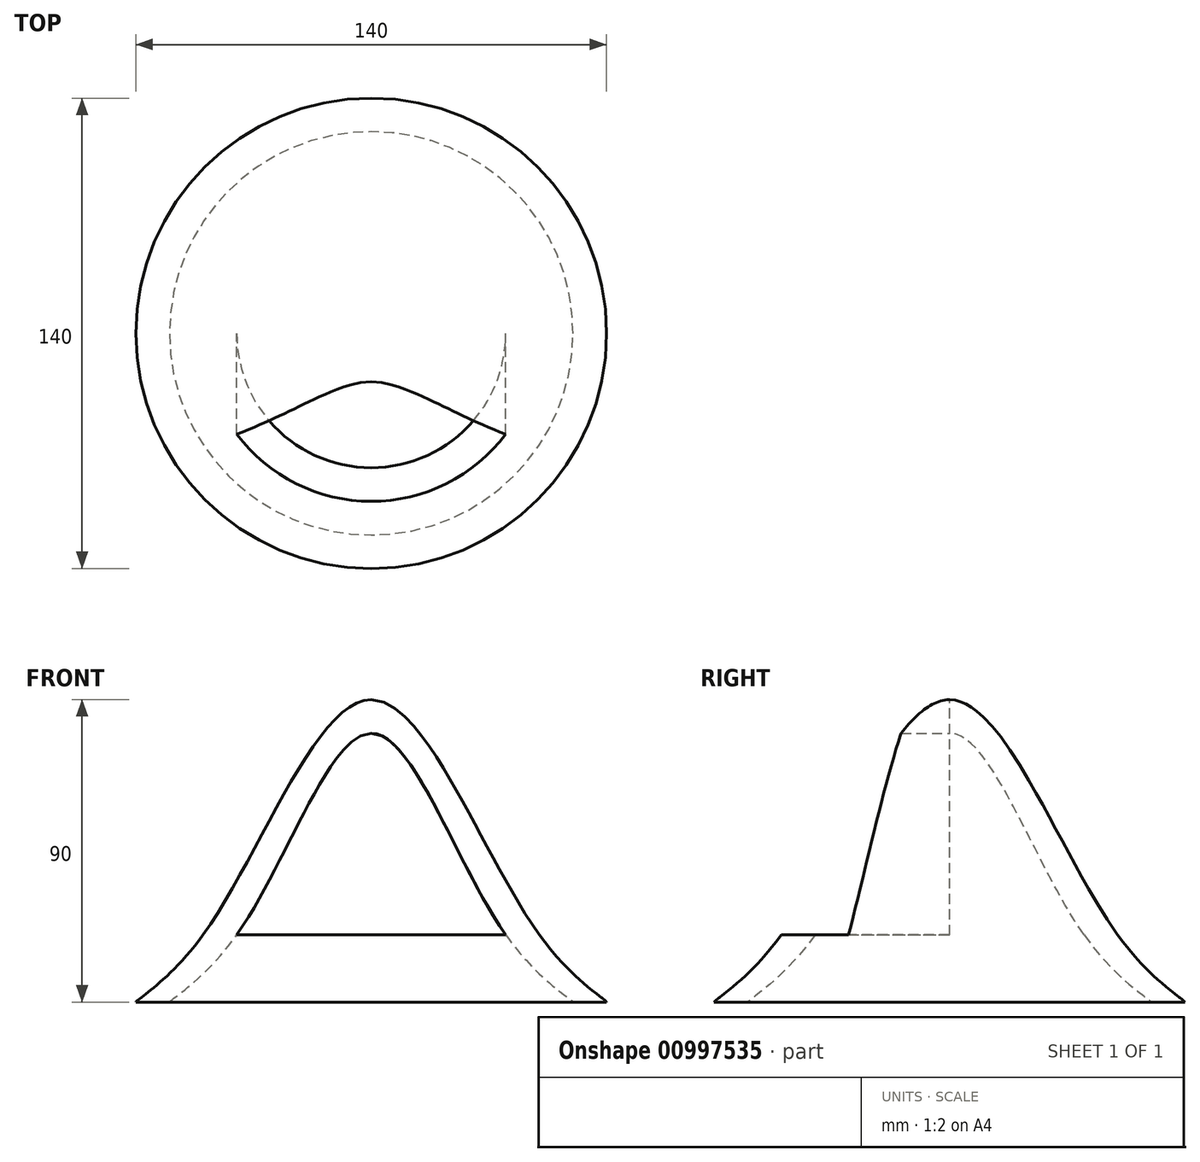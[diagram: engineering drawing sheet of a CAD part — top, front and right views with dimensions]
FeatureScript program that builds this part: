
annotation { "Feature Type Name" : "Feature", "Feature Type Description" : "" }
export const myFeature = defineFeature(function(context is Context, id is Id, definition is map)
    precondition{}
    {
        {
            var Q0;
            Q0=qCreatedBy(makeId("Front.planeOp"),FACE);
            var sketch = newSketch(context, id + "F0", { "sketchPlane" : qUnion([Q0])});
            skLineSegment(sketch, "E0", {"start": v(-40, 20) * mm, "end": v(0, 20) * mm});
            skLineSegment(sketch, "E1", {"start": v(0, 0) * mm, "end": v(0, 20) * mm});
            skLineSegment(sketch, "E2", {"start": v(0, 20) * mm, "end": v(0, 80) * mm});
            skLineSegment(sketch, "E3", {"start": v(0, 80) * mm, "end": v(0, 90) * mm});
            skLineSegment(sketch, "E4", {"start": v(-70, 0) * mm, "end": v(-60, 0) * mm});
            skLineSegment(sketch, "E5", {"start": v(-60, 0) * mm, "end": v(0, 0) * mm});
            skLineSegment(sketch, "E6", {"start": v(-40, 20) * mm, "end": v(-50, 20) * mm});
            skLineSegment(sketch, "E7.MirrorCS", {"start": v(40, 20) * mm, "end": v(0, 20) * mm});
            skLineSegment(sketch, "E8.MirrorCS", {"start": v(40, 20) * mm, "end": v(50, 20) * mm});
            skLineSegment(sketch, "E9.MirrorCS", {"start": v(60, 0) * mm, "end": v(0, 0) * mm});
            skLineSegment(sketch, "E10.MirrorCS", {"start": v(70, 0) * mm, "end": v(60, 0) * mm});
            skFitSpline(sketch, "E11", {"points": [v(-70, 0) * mm, v(-50, 20) * mm, v(0, 90) * mm, v(50, 20) * mm, v(70, 0) * mm], "startDerivative": vector(11.68, 19) * mm, "endDerivative": vector(11.68, -19) * mm});
            skFitSpline(sketch, "E12", {"points": [v(-60, 0) * mm, v(-40, 20) * mm, v(0, 80) * mm, v(40, 20) * mm, v(60, 0) * mm], "startDerivative": vector(11.83, 17.83) * mm, "endDerivative": vector(11.83, -17.83) * mm});
            skSolve(sketch);
        }
        {
            var Q0;
            {var subQ0=sQuery(id+"F0.wireOp",EDGE,"E4");Q0=makeQuery(id+"F0.imprint","IMPRINT",FACE,{"disambiguationData":[TD([[makeQuery(id+"F0.imprint","IMPRINT",EDGE,{"derivedFrom":subQ0}),1.0]])]});}
            var Q1;
            {var subQ0=sQuery(id+"F0.wireOp",EDGE,"E3");Q1=makeQuery(id+"F0.imprint","IMPRINT",FACE,{"disambiguationData":[TD([[makeQuery(id+"F0.imprint","IMPRINT",EDGE,{"derivedFrom":subQ0}),1.0]])]});}
            var Q2;
            Q2=sQuery(id+"F0.wireOp",EDGE,"E4");
            var Q3;
            Q3=sQuery(id+"F0.wireOp",EDGE,"E11");
            var Q4;
            Q4=sQuery(id+"F0.wireOp",EDGE,"E10.MirrorCS");
            var Q5;
            Q5=sQuery(id+"F0.wireOp",EDGE,"E12");
            var Q6;
            Q6=sQuery(id+"F0.wireOp",EDGE,"E2");
            revolve(context, id + "F1", {"surfaceOperationType" : NewSurfaceOperationType.NEW, "entities" : qUnion([Q0, Q1]), "surfaceEntities" : qUnion([Q2, Q3, Q4, Q5]), "axis" : qUnion([Q6]), "revolveType" : RevolveType.FULL});
        }
        {
            var Q0;
            {var subQ0=sQuery(id+"F0.wireOp",EDGE,"E2");Q0=makeQuery(id+"F0.imprint","IMPRINT",FACE,{"disambiguationData":[TD([[makeQuery(id+"F0.imprint","IMPRINT",EDGE,{"derivedFrom":subQ0}),-1.0]])]});}
            var Q1;
            {var subQ0=sQuery(id+"F0.wireOp",EDGE,"E0");Q1=makeQuery(id+"F0.imprint","IMPRINT",FACE,{"disambiguationData":[TD([[makeQuery(id+"F0.imprint","IMPRINT",EDGE,{"derivedFrom":subQ0}),1.0]])]});}
            extrude(context, id + "F2", {"entities" : qUnion([Q0, Q1]), "operationType" : NewBodyOperationType.REMOVE, "endBound" : BoundingType.THROUGH_ALL, "depth" : 50.8 * mm, "offsetDistance" : 25.4 * mm});
        }
    });
